# Revit family: Hitachi_CSNET-Lite_LOD400
name_source: partatom
category: Equipement électrique
revit_build: Autodesk Revit 2018 (Build: 20181015_0930(x64)
units: mm (PartAtom-declared; Revit-internal decimal feet)

## family parameters
Basée sur le plan de construction = Non
Configuration du panneau = Deux colonnes, circuits au sein
Cote de connecteur circulaire = Utiliser le diamètre
Couper avec des vides une fois chargée = Non
Partagée = Non
Point de calcul de pièce = Non
Toujours verticalement = Oui
Type d'élément = Tableau de raccordement

## types (1)
- CSNET Lite
    BC_OBJECT_ID = 219734
    BC_OBJECT_VERSION = #2
    BC_VARIANT_ID = 582327
    Communication Type = HLINK and TCP/IP
    Consumption = 5 W
    Fabricant = Hitachi Air Conditioning Europe SAS
    Frequency = 50 Hz
    Gross Weight = 0.27 kg
    Insulation Standard Class = ClassIIAppliance
    MasterFormat = Electric and Electronic Control System for HVAC
    Masterformat Code = 23 09 33
    Maximum Current = 0 A
    Maximum Operating Temperature = 40 °C
    Maximum connection distance = 100 m
    Minimum Operating Temperature = 0 °C
    Modèle = CSNET Lite
    Nominal Voltage = 230 V
    Number of Phases = 1
    OmniClass code = 23-27 15 23 11
    OmniClass description = HVAC Main Control Panels
    Overall depth = 171 mm  [stored 0.561024 ft]
    Overall height = 88 mm  [stored 0.288714 ft]
    Overall width = 107 mm  [stored 0.35105 ft]
    Product Code = 7E512205
    Rated Power (kW) = 5 W
    Reference = CSNET Lite
    Type of Electrical Connectors = RJ45, USB mini, USB standard
    Uniformat = Other Controls & Instrumentation
    Uniformat code = D306002

note: [stored X ft] marks values corroborated as IEEE doubles in the binary element streams (Revit-internal decimal feet)
